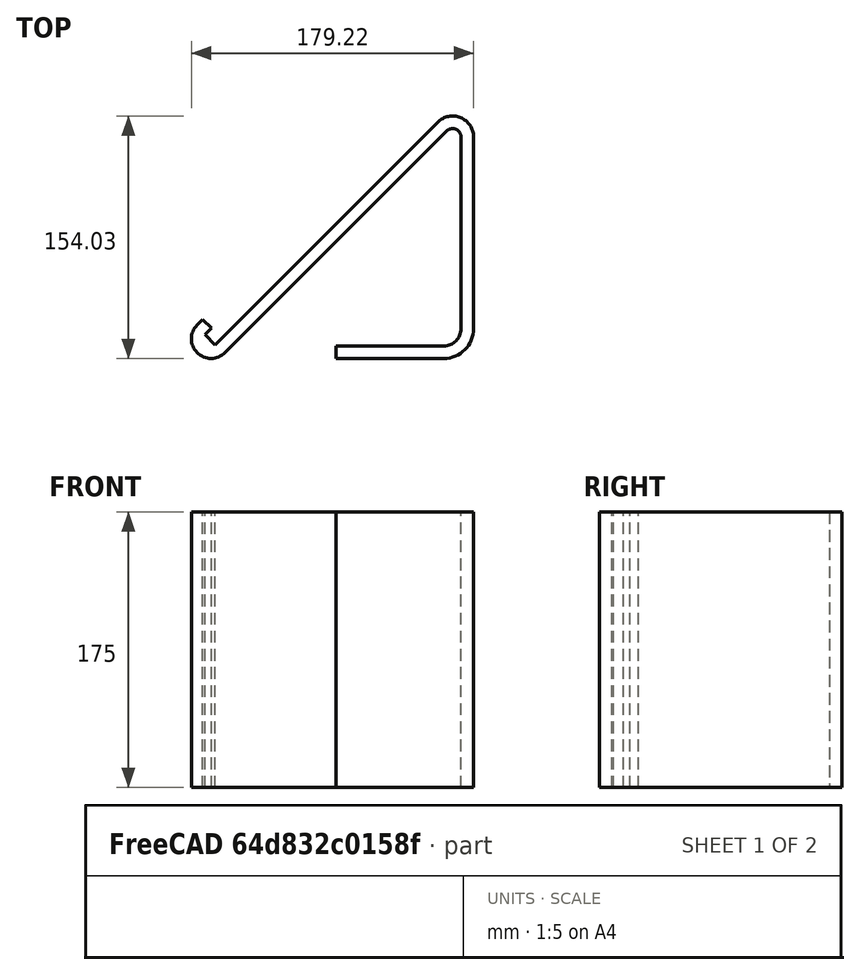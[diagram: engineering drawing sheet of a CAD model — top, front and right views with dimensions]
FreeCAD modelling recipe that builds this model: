
FCSTD DOCUMENT  (FreeCAD 0.17RUnknown)
Label: aaa
License: All rights reserved
LicenseURL: http://en.wikipedia.org/wiki/All_rights_reserved
objects: Sketcher::SketchObject×1, PartDesign::Pad×1, PartDesign::Body×1
note: 4 computed .brp shape members not serialized (recipe doc carries the construction recipe); baked Part::Feature solids carry a one-line shape summary decoded from their .brp

FEATURE [Sketcher::SketchObject] Sketch
  MapMode = 5
  Support = -> [XY_Plane]
  sketch-geometry (16):
    g0: LineSegment StartX=8.4682 StartY=3.65567 StartZ=0 EndX=149.28 EndY=144.468 EndZ=0
    g1: LineSegment StartX=158.353 StartY=140.71 StartZ=0 EndX=158.353 EndY=18.9037 EndZ=0
    g2: LineSegment StartX=147.449 StartY=8 StartZ=0 EndX=79.105 EndY=8 EndZ=0
    g3: LineSegment StartX=79.105 StartY=8 StartZ=0 EndX=79.105 EndY=0 EndZ=0
    g4: LineSegment StartX=79.105 StartY=0 StartZ=0 EndX=147.449 EndY=0 EndZ=0
    g5: LineSegment StartX=166.353 StartY=18.9037 StartZ=0 EndX=166.353 EndY=140.71 EndZ=0
    g6: LineSegment StartX=143.623 StartY=150.125 StartZ=0 EndX=2.20208 EndY=8.70326 EndZ=0
    g7: LineSegment StartX=-4.16188 StartY=15.0672 StartZ=0 EndX=-0.0170831 EndY=19.212 EndZ=0
    g8: LineSegment StartX=-0.0170831 StartY=19.212 StartZ=0 EndX=-5.67394 EndY=24.8689 EndZ=0
    g9: LineSegment StartX=-5.67394 StartY=24.8689 StartZ=0 EndX=-9.20947 EndY=21.3333 EndZ=0
    g10: ArcOfCircle CenterX=153.038 CenterY=140.71 CenterZ=0 NormalX=0 NormalY=0 NormalZ=1 AngleXU=0 Radius=5.31443 StartAngle=0 EndAngle=2.35619
    g11: ArcOfCircle CenterX=153.038 CenterY=140.71 CenterZ=0 NormalX=0 NormalY=0 NormalZ=1 AngleXU=0 Radius=13.3144 StartAngle=0 EndAngle=2.35619
    g12: ArcOfCircle CenterX=147.449 CenterY=18.9037 CenterZ=0 NormalX=0 NormalY=0 NormalZ=1 AngleXU=0 Radius=10.9037 StartAngle=4.71239 EndAngle=6.28319
    g13: ArcOfCircle CenterX=147.449 CenterY=18.9037 CenterZ=0 NormalX=0 NormalY=0 NormalZ=1 AngleXU=0 Radius=18.9037 StartAngle=4.71239 EndAngle=6.28319
    g14: ArcOfCircle CenterX=-0.370636 CenterY=12.4945 CenterZ=0 NormalX=0 NormalY=0 NormalZ=1 AngleXU=0 Radius=12.5 StartAngle=2.35619 EndAngle=5.49779
    g15: LineSegment StartX=-4.16188 StartY=15.0672 StartZ=0 EndX=2.20208 EndY=8.70326 EndZ=0
  constraints (36):
    c: Vertical(g1)
    c: Horizontal(g2)
    c: Coincident(g2,g3)
    c: Vertical(g3)
    c: Coincident(g3,g4)
    c: Coincident(g7,g8)
    c: Coincident(g8,g9)
    c: Tangent(g1,g10) = 1.5708
    c: Tangent(g0,g10) = 1.5708
    c: Tangent(g6,g11) = -1.5708
    c: Tangent(g5,g11) = -1.5708
    c: Tangent(g1,g12) = 1.5708
    c: Tangent(g2,g12) = 1.5708
    c: Tangent(g4,g13) = -1.5708
    c: Tangent(g5,g13) = -1.5708
    c: Tangent(g9,g14) = -1.5708
    c: Tangent(g0,g14) = -1.5708
    c: Coincident(g10,g11)
    c: Coincident(g13,g12)
    c: Parallel(g0,g6)
    c: Parallel(g1,g5)
    c: Parallel(g2,g4)
    c: Parallel(g7,g9)
    c: Parallel(g7,g6)
    c: PointOnObject(g-1,g14)
    c: PointOnObject(g3,g-1)
    c: Perpendicular(g8,g9)
    c: Distance(g8) = 8
    c: Distance(g6) = 200
    c: Coincident(g15,g7)
    c: Coincident(g15,g6)
    c: Distance(g15) = 9
    c: Perpendicular(g15,g7)
    c: Distance(g0,g6) = 8
    c: Distance(g9) = 5
    c: Angle(g11) = 2.35619
FEATURE [PartDesign::Pad] Pad002
  Length = 175
  Length2 = 100
  Profile = -> Sketch
  Type = 0
FEATURE [PartDesign::Body] Body
  Group = -> [Sketch,Pad002]
  Origin = -> Origin
  Tip = -> Pad002
